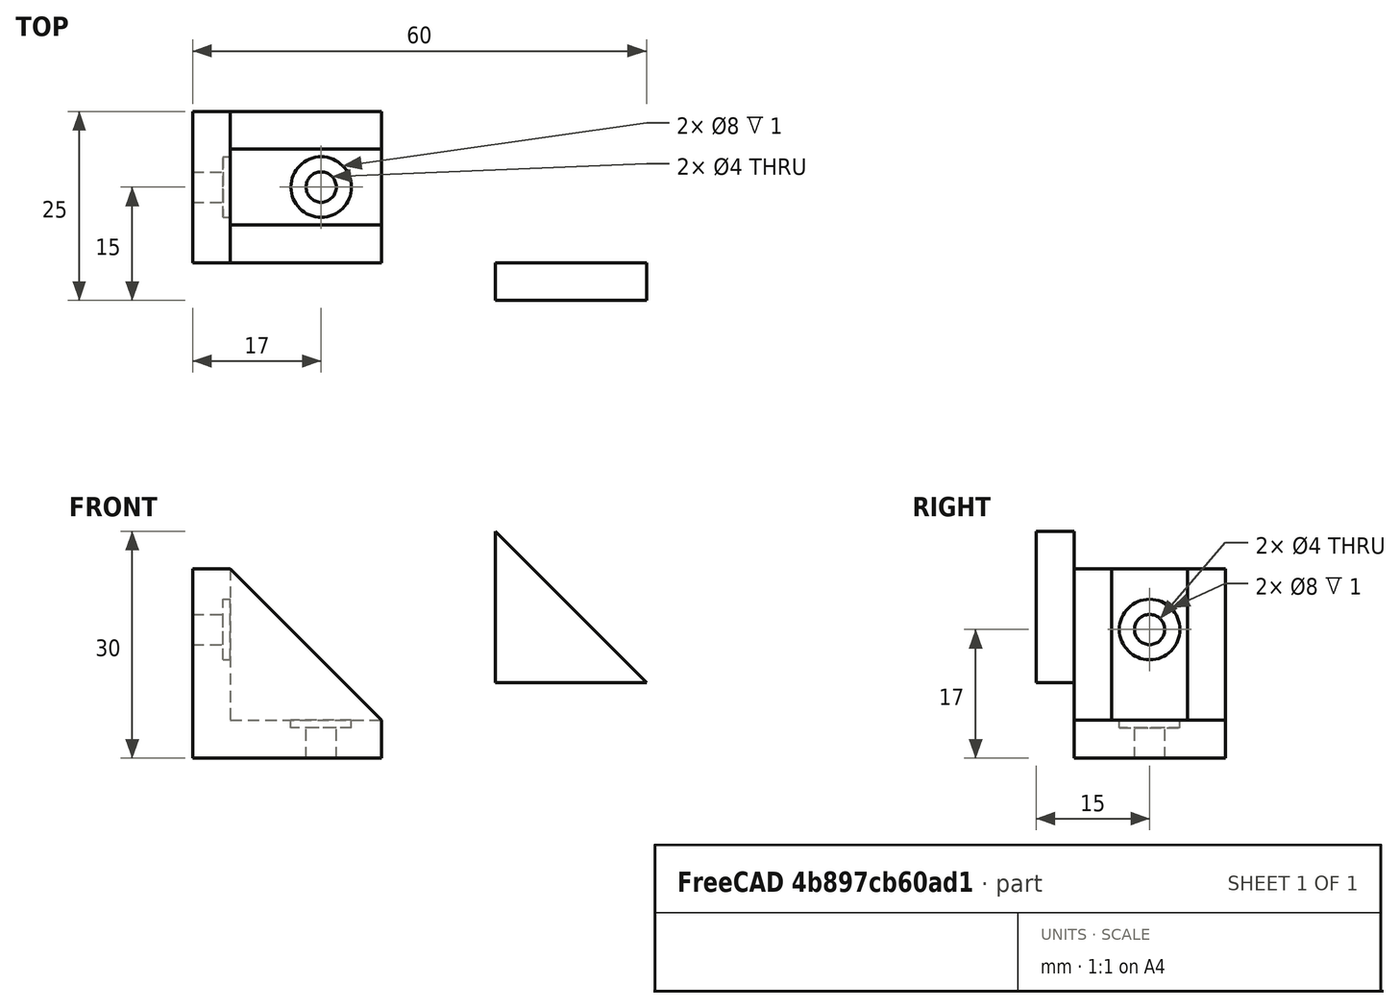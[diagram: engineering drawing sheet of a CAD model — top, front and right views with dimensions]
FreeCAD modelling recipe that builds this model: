
FCSTD DOCUMENT  (FreeCAD 0.18R14555 (Git shallow))
Label: corner-bracket
License: All rights reserved
LicenseURL: http://en.wikipedia.org/wiki/All_rights_reserved
objects: Part::Cylinder×4, Part::Feature×4, Part::MultiFuse×3, Part::Box×2, Part::Cut×1, Sketcher::SketchObject×1, PartDesign::Pad×1, PartDesign::Body×1
note: 18 computed .brp shape members not serialized (recipe doc carries the construction recipe); baked Part::Feature solids carry a one-line shape summary decoded from their .brp

FEATURE [Part::Box] Box  label="Cube"
  AttacherType = Attacher::AttachEngine3D
  Height = 25
  Length = 5
  Width = 20
FEATURE [Part::Box] Box001  label="Cube001"
  AttacherType = Attacher::AttachEngine3D
  Height = 5
  Length = 25
  Width = 20
FEATURE [Part::Cylinder] Cylinder
  Angle = 360
  AttacherType = Attacher::AttachEngine3D
  Height = 1
  Placement = pos=(17,10,4) rot=(0,0,1;0rad)
  Radius = 4
FEATURE [Part::Cylinder] Cylinder001
  Angle = 360
  AttacherType = Attacher::AttachEngine3D
  Height = 1
  Placement = pos=(4,10,17) rot=(0,1,0;1.5708rad)
  Radius = 4
FEATURE [Part::Cylinder] Cylinder002
  Angle = 360
  AttacherType = Attacher::AttachEngine3D
  Height = 5
  Placement = pos=(-4e-15,10,17) rot=(0,1,0;1.5708rad)
  Radius = 2
FEATURE [Part::Cylinder] Cylinder003
  Angle = 360
  AttacherType = Attacher::AttachEngine3D
  Height = 5
  Placement = pos=(17,10,0) rot=(0,0,1;0rad)
  Radius = 2
FEATURE [Part::MultiFuse] Fusion
  Shapes = -> [Cylinder003,Cylinder002,Cylinder001,Cylinder]
FEATURE [Part::MultiFuse] Fusion001
  Shapes = -> [Box001,Box]
FEATURE [Part::Cut] Cut
  Base = -> Fusion001
  Tool = -> Fusion
FEATURE [Sketcher::SketchObject] Sketch
  MapMode = 5
  Placement = pos=(0,0,0) rot=(1,0,0;1.5708rad)
  Support = -> [XZ_Plane]
  sketch-geometry (3):
    g0: LineSegment StartX=40 StartY=30 StartZ=0 EndX=40 EndY=10 EndZ=0
    g1: LineSegment StartX=40 StartY=10 StartZ=0 EndX=60 EndY=10 EndZ=0
    g2: LineSegment StartX=60 StartY=10 StartZ=0 EndX=40 EndY=30 EndZ=0
  constraints (4):
    c: Vertical(g0)
    c: Coincident(g0,g1)
    c: Horizontal(g1)
    c: Coincident(g1,g2)
FEATURE [PartDesign::Pad] Pad
  Length = 5
  Length2 = 100
  Placement = pos=(0,0,0) rot=(1,0,0;1.5708rad)
  Profile = -> Sketch
  Type = 0
FEATURE [PartDesign::Body] Body
  Group = -> [Sketch,Pad]
  Origin = -> Origin
  Tip = -> Pad
FEATURE [Part::Feature] Body001
  Placement = pos=(-35,5,-5) rot=(0,0,1;0rad)
  shape: bbox 20 x 5 x 20 mm, 5 faces (baked)
FEATURE [Part::Feature] Body002
  Placement = pos=(-35,20,-5) rot=(0,0,1;0rad)
  shape: bbox 20 x 5 x 20 mm, 5 faces (baked)
FEATURE [Part::MultiFuse] Fusion002
  Shapes = -> [Body002,Body001,Cut]
FEATURE [Part::Feature] Fusion002001  label="Fusion003"
  shape: bbox 25 x 20 x 25 mm, 18 faces (baked)
FEATURE [Part::Feature] Fusion002001_solid  label="Fusion003 (Solid)"
  shape: bbox 25 x 20 x 25 mm, 18 faces (baked)
